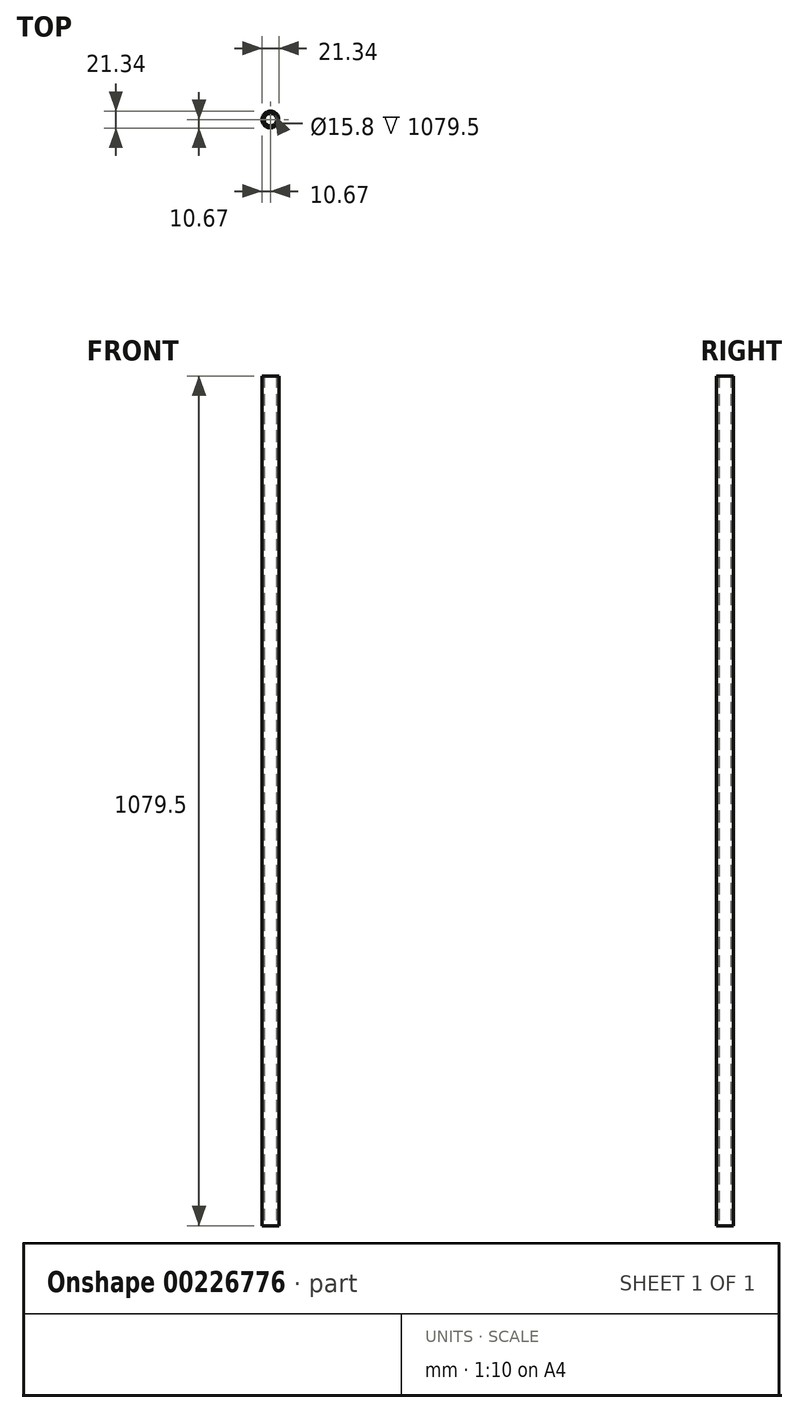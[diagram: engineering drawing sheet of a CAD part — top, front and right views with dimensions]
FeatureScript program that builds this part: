
annotation { "Feature Type Name" : "Feature", "Feature Type Description" : "" }
export const myFeature = defineFeature(function(context is Context, id is Id, definition is map)
    precondition{}
    {
        {
            var Q0;
            Q0=qCreatedBy(makeId("Top.planeOp"),FACE);
            var sketch = newSketch(context, id + "F0", { "sketchPlane" : qUnion([Q0])});
            skCircle(sketch, "E0", {"center": v(0, 0) * mm, "radius": 10.67 * mm});
            skCircle(sketch, "E1", {"center": v(0, 0) * mm, "radius": 7.9 * mm});
            skSolve(sketch);
        }
        {
            var Q0;
            Q0=makeQuery(id+"F0.imprint","IMPRINT",FACE,{"disambiguationData":[TD([[makeQuery(id+"F0.imprint","IMPRINT",EDGE,{"derivedFrom":sQuery(id+"F0.wireOp",EDGE,"E0")}),1.0]])]});
            extrude(context, id + "F1", {"entities" : qUnion([Q0]), "depth" : 1079.5 * mm, "offsetDistance" : 25 * mm});
        }
    });
